# Revit family: HB450VJ3.1
name_source: partatom
category: HLS-Bauteile
revit_build: Autodesk Revit 2016 (Build: 20150714_1515(x64)
units: mm (PartAtom-declared; Revit-internal decimal feet)

## family parameters
Arbeitsebenenbasiert = Nein
Beim Laden mit Abzugskörper schneiden = Nein
Bemaßung runder Anschluss = Durchmesser verwenden
Gemeinsam genutzt = Nein
Immer vertikal = Ja
OmniClass-Nummer = 23.75.10.21
OmniClass-Titel = Heat Pumps
Raumberechnungspunkt = Nein
Teiletyp = Normal

## types (1)
- HB450VJ3.1
    ALG_Empfohlene_Wasservorlage_in_l/kW = 16
    ALG_Gewicht_in_kg = 185
    ALG_ManufacturerCode = HB450VJ3.1
    ALG_Schalldruckpegel_Nominal_in_dB(A) = 33
    ALG_Umgebungsbedingungen = +5 bis +35 °C
    Beschreibung = Hydrobox
    HLS_Bezeichnung_1 = Hydrobox
    HLS_Bezeichnung_2 = HB450VJ3.1
    HLS_Breite = 675 mm  [stored 2.21457 ft]
    HLS_Höhe = 1100 mm
    HLS_Länge = 1020 mm  [stored 3.34646 ft]
    HLS_Typ = HB450VJ3.1
    Hersteller = YANMAR
    Modell = HB450VJ3.1
    Nenndruckverlust (Heizen) in kPa = 15
    Nennleistung (Heizen) in kW = 46,3
    Nennleistung (Kühlen) in kW = 36,3
    Nennvolumenstrom (Heizen) in m3/h = 8
    Typenkommentare = Hydrobox
    URL = www.energysystem-yanmar.com

note: [stored X ft] marks values corroborated as IEEE doubles in the binary element streams (Revit-internal decimal feet)

## geometry (parser evidence)
native form markers: Blend x9, Sweep x3
no freeform markers — native parametric forms only
